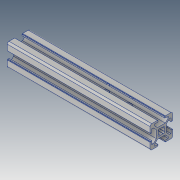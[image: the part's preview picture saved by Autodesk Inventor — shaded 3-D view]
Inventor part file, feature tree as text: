
AUTODESK INVENTOR PART (.ipt)
format: ipt  version: 2018.2 (Build 222227000, 227)  size: 239,616 bytes
history: native  units: mm
features: sketch x2, other x1, extrude x1, hole x1
ambient origin geometry x8: Origin, YZ Plane, XZ Plane, XY Plane, X Axis, Y Axis, Z Axis, Center Point
bodies: Body1 (feature_tree)
feature tree (5):
  other  "90-50-PROFILES-20x20xSketch.ipt"
  extrude  "Extrusion3"  Depth=10.0mm TaperAngle=0.0deg
  hole  "Bohrung2"  [1 undecoded]
  sketch  "Skizze2"  dims[d6=10.0mm d7=126.0mm d8=0.0mm]
  sketch  "Skizze6"  dims[d18=30.0mm d19=20.0mm d20=6.5mm d21=6.0mm d22=4.0mm d23=2.0mm d24=90.0deg d25=8.0mm d26=20.594885mm]
note: 1 required parameter value undecoded (feature->parameter linkage not recoverable at this tier; creation-order binding heuristic only, values carry confidence <= 0.55)
